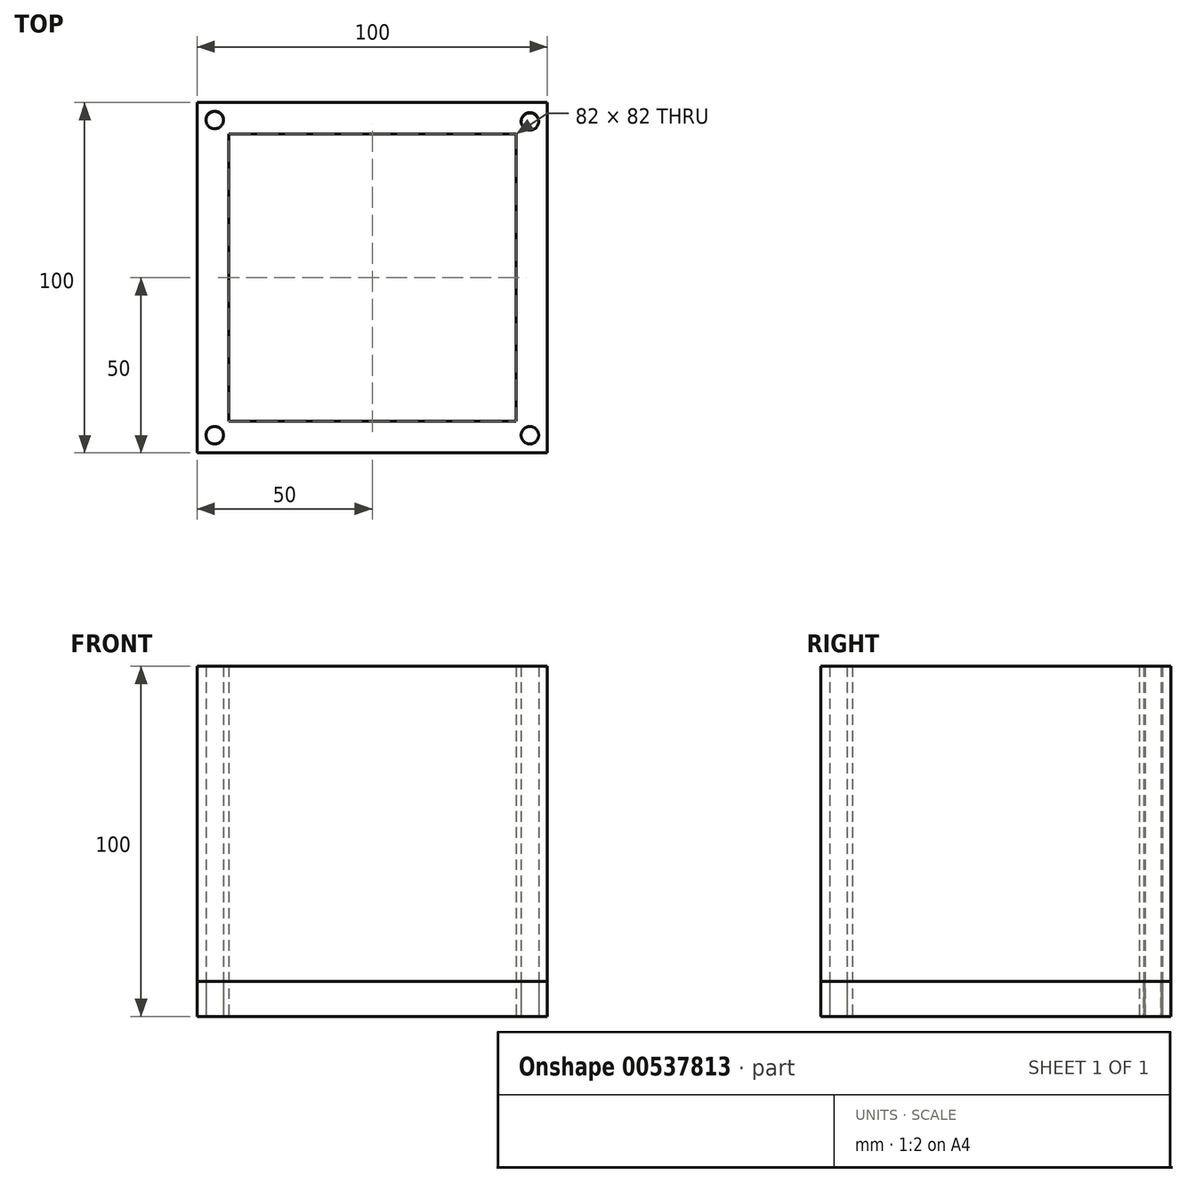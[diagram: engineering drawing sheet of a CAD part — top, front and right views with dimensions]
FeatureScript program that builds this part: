
annotation { "Feature Type Name" : "Feature", "Feature Type Description" : "" }
export const myFeature = defineFeature(function(context is Context, id is Id, definition is map)
    precondition{}
    {
        {
            var Q0;
            Q0=qCreatedBy(makeId("Top.planeOp"),FACE);
            var sketch = newSketch(context, id + "F0", { "sketchPlane" : qUnion([Q0])});
            skLineSegment(sketch, "E0.bottom", {"start": v(50, 50) * mm, "end": v(-50, 50) * mm});
            skLineSegment(sketch, "E0.top", {"start": v(50, -50) * mm, "end": v(-50, -50) * mm});
            skLineSegment(sketch, "E0.left", {"start": v(50, 50) * mm, "end": v(50, -50) * mm});
            skLineSegment(sketch, "E0.right", {"start": v(-50, 50) * mm, "end": v(-50, -50) * mm});
            skPoint(sketch, "E0.middle", {"position": v(0, 0) * mm});
            skCircle(sketch, "E1", {"center": v(45, -45) * mm, "radius": 2.5 * mm});
            skCircle(sketch, "E2", {"center": v(-45, 45) * mm, "radius": 2.5 * mm});
            skCircle(sketch, "E3", {"center": v(45, 44.58) * mm, "radius": 2.5 * mm});
            skCircle(sketch, "E4", {"center": v(-45, -45) * mm, "radius": 2.5 * mm});
            skSolve(sketch);
        }
        {
            var Q0;
            Q0 = qSketchRegion(id + "F0", true);
            extrude(context, id + "F1", {"entities" : qUnion([Q0]), "depth" : 10 * mm, "offsetDistance" : 25 * mm});
        }
        {
            var Q0;
            Q0=qCreatedBy(makeId("Top.planeOp"),FACE);
            var sketch = newSketch(context, id + "F2", { "sketchPlane" : qUnion([Q0])});
            skLineSegment(sketch, "E5.bottom", {"start": v(-50, -50) * mm, "end": v(50, -50) * mm});
            skLineSegment(sketch, "E5.top", {"start": v(-50, 50) * mm, "end": v(50, 50) * mm});
            skLineSegment(sketch, "E5.left", {"start": v(-50, -50) * mm, "end": v(-50, 50) * mm});
            skLineSegment(sketch, "E5.right", {"start": v(50, -50) * mm, "end": v(50, 50) * mm});
            skPoint(sketch, "E5.middle", {"position": v(0, 0) * mm});
            skCircle(sketch, "E6", {"center": v(-45, 45.06) * mm, "radius": 2.5 * mm});
            skCircle(sketch, "E7", {"center": v(45, 44.65) * mm, "radius": 2.5 * mm});
            skCircle(sketch, "E8", {"center": v(-45, -45) * mm, "radius": 2.5 * mm});
            skCircle(sketch, "E9", {"center": v(45, -45) * mm, "radius": 2.5 * mm});
            skLineSegment(sketch, "E10.bottom", {"start": v(-41, -41) * mm, "end": v(41, -41) * mm});
            skLineSegment(sketch, "E10.top", {"start": v(-41, 41) * mm, "end": v(41, 41) * mm});
            skLineSegment(sketch, "E10.left", {"start": v(-41, -41) * mm, "end": v(-41, 41) * mm});
            skLineSegment(sketch, "E10.right", {"start": v(41, -41) * mm, "end": v(41, 41) * mm});
            skSolve(sketch);
        }
        {
            var Q0;
            Q0 = qSketchRegion(id + "F2", true);
            extrude(context, id + "F3", {"entities" : qUnion([Q0]), "depth" : 100 * mm, "offsetDistance" : 25 * mm});
        }
    });
